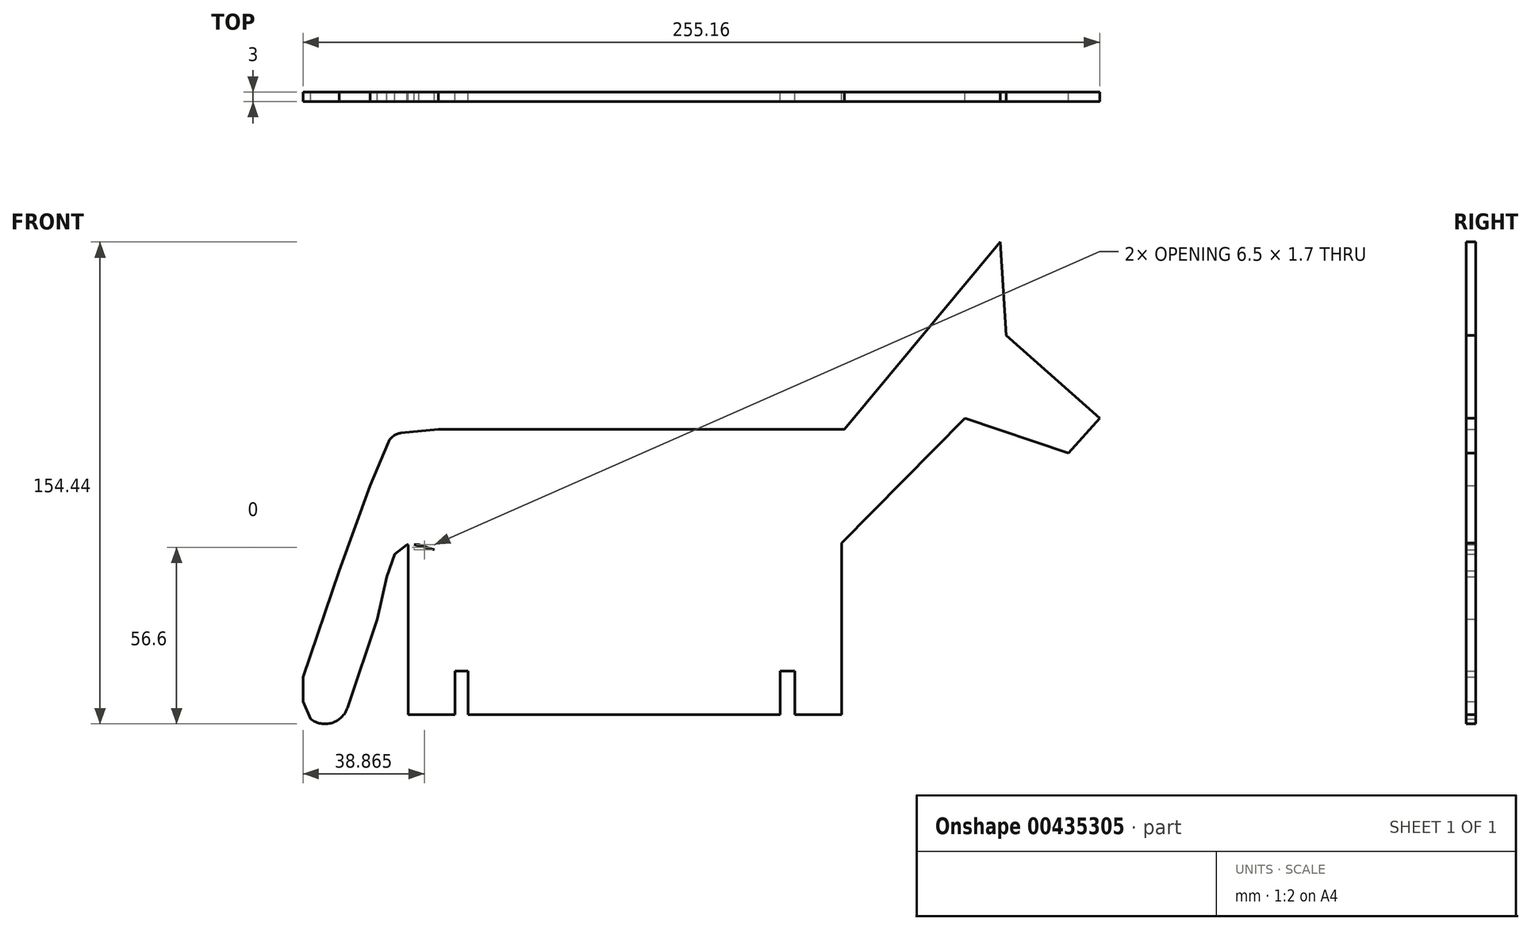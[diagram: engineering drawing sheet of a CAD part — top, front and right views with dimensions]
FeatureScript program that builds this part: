
annotation { "Feature Type Name" : "Feature", "Feature Type Description" : "" }
export const myFeature = defineFeature(function(context is Context, id is Id, definition is map)
    precondition{}
    {
        {
            var Q0;
            Q0=qCreatedBy(makeId("Front.planeOp"),FACE);
            var sketch = newSketch(context, id + "F0", { "sketchPlane" : qUnion([Q0])});
            skLineSegment(sketch, "E0", {"start": v(-77.3, 67.96) * mm, "end": v(52.7, 67.96) * mm});
            skLineSegment(sketch, "E1", {"start": v(52.7, 67.96) * mm, "end": v(102.7, 127.96) * mm});
            skLineSegment(sketch, "E2", {"start": v(102.7, 127.96) * mm, "end": v(102.7, 127.96) * mm});
            skLineSegment(sketch, "E3", {"start": v(102.7, 127.96) * mm, "end": v(104.55, 98.01) * mm});
            skLineSegment(sketch, "E4", {"start": v(104.55, 98.01) * mm, "end": v(134.49, 71.48) * mm});
            skLineSegment(sketch, "E5", {"start": v(134.49, 71.48) * mm, "end": v(124.54, 60.26) * mm});
            skLineSegment(sketch, "E6", {"start": v(124.54, 60.26) * mm, "end": v(91.39, 71.48) * mm});
            skLineSegment(sketch, "E7", {"start": v(91.39, 71.48) * mm, "end": v(51.8, 31.48) * mm});
            skLineSegment(sketch, "E8", {"start": v(51.8, 31.48) * mm, "end": v(51.8, -23.52) * mm});
            skLineSegment(sketch, "E9", {"start": v(51.8, -23.52) * mm, "end": v(36.8, -23.52) * mm});
            skLineSegment(sketch, "E10", {"start": v(36.8, -23.52) * mm, "end": v(36.8, -9.52) * mm});
            skLineSegment(sketch, "E11", {"start": v(36.8, -9.52) * mm, "end": v(32.2, -9.52) * mm});
            skLineSegment(sketch, "E12", {"start": v(32.2, -9.52) * mm, "end": v(32.2, -23.52) * mm});
            skLineSegment(sketch, "E13", {"start": v(32.2, -23.52) * mm, "end": v(-67.8, -23.52) * mm});
            skLineSegment(sketch, "E14", {"start": v(-67.8, -23.52) * mm, "end": v(-67.8, -9.52) * mm});
            skLineSegment(sketch, "E15", {"start": v(-67.8, -9.52) * mm, "end": v(-72.02, -9.52) * mm});
            skLineSegment(sketch, "E16", {"start": v(-72.02, -9.52) * mm, "end": v(-72.02, -23.52) * mm});
            skLineSegment(sketch, "E17", {"start": v(-72.02, -23.52) * mm, "end": v(-87.02, -23.52) * mm});
            skLineSegment(sketch, "E18", {"start": v(-87.02, -23.52) * mm, "end": v(-87.02, 31.48) * mm});
            skLineSegment(sketch, "E19", {"start": v(-87.02, 31.48) * mm, "end": v(-78.56, 29.27) * mm});
            skLineSegment(sketch, "E20", {"start": v(-78.56, 29.27) * mm, "end": v(-83.57, 30.97) * mm});
            skLineSegment(sketch, "E21", {"start": v(-83.57, 30.97) * mm, "end": v(-87.4, 30.97) * mm});
            skLineSegment(sketch, "E22", {"start": v(-87.4, 30.97) * mm, "end": v(-91.35, 27.96) * mm});
            skLineSegment(sketch, "E23", {"start": v(-91.35, 27.96) * mm, "end": v(-93.83, 20.64) * mm});
            skLineSegment(sketch, "E24", {"start": v(-93.83, 20.64) * mm, "end": v(-96.82, 7.08) * mm});
            skLineSegment(sketch, "E25", {"start": v(-96.82, 7.08) * mm, "end": v(-106.44, -21.33) * mm});
            skArc(sketch, "E26", {"start": v(-118.21, -24.93) * mm, "mid": v(-111.4, -26.15) * mm, "end": v(-106.44, -21.33) * mm});
            skLineSegment(sketch, "E27", {"start": v(-118.21, -24.93) * mm, "end": v(-120.67, -19.33) * mm});
            skLineSegment(sketch, "E28", {"start": v(-120.67, -19.33) * mm, "end": v(-120.67, -11.5) * mm});
            skLineSegment(sketch, "E29", {"start": v(-120.67, -11.5) * mm, "end": v(-109.09, 22.58) * mm});
            skLineSegment(sketch, "E30", {"start": v(-109.09, 22.58) * mm, "end": v(-99.2, 49.85) * mm});
            skLineSegment(sketch, "E31", {"start": v(-99.2, 49.85) * mm, "end": v(-93.37, 63.7) * mm});
            skLineSegment(sketch, "E32", {"start": v(-89.26, 66.74) * mm, "end": v(-77.3, 67.96) * mm});
            skPoint(sketch, "E33.visualSharp", {"position": v(-92.22, 66.44) * mm});
            skArc(sketch, "E33.filletArc", {"start": v(-89.26, 66.74) * mm, "mid": v(-91.73, 65.78) * mm, "end": v(-93.37, 63.7) * mm});
            skSolve(sketch);
        }
        {
            var Q0;
            Q0 = qSketchRegion(id + "F0", true);
            extrude(context, id + "F1", {"entities" : qUnion([Q0]), "depth" : 3 * mm});
        }
        {
            var Q0;
            Q0 = qSketchRegion(id + "F0", true);
            extrude(context, id + "F2", {"entities" : qUnion([Q0]), "depth" : 3 * mm});
        }
    });
